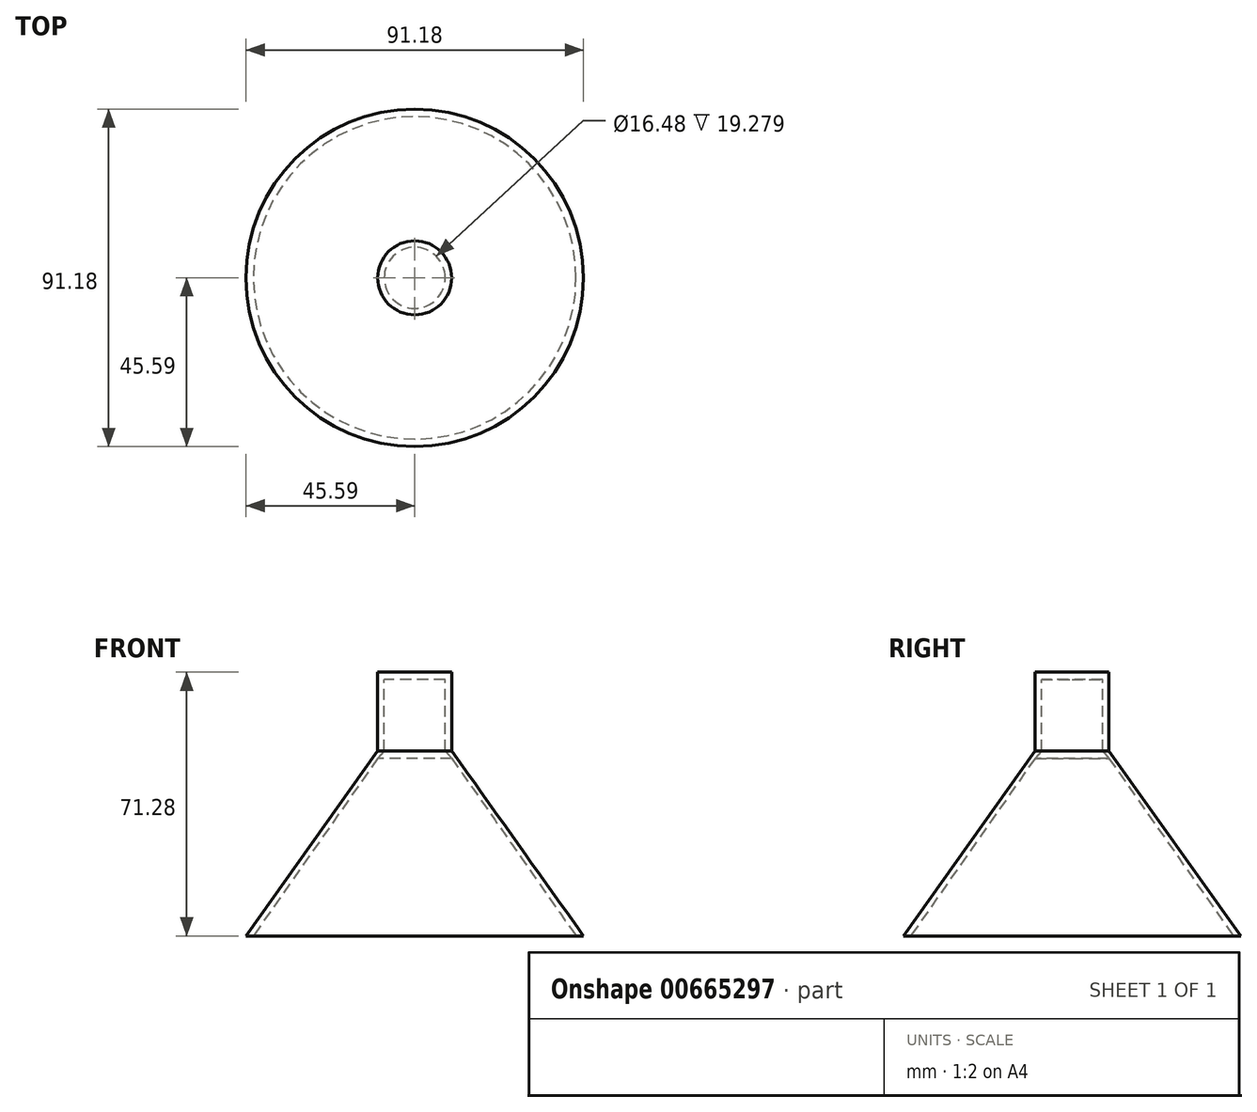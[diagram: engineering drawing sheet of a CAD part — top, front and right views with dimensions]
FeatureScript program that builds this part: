
annotation { "Feature Type Name" : "Feature", "Feature Type Description" : "" }
export const myFeature = defineFeature(function(context is Context, id is Id, definition is map)
    precondition{}
    {
        {
            var Q0;
            Q0=qCreatedBy(makeId("Front.planeOp"),FACE);
            var sketch = newSketch(context, id + "F0", { "sketchPlane" : qUnion([Q0])});
            skLineSegment(sketch, "E0", {"start": v(-10, 50) * mm, "end": v(-45.59, 0) * mm});
            skLineSegment(sketch, "E1", {"start": v(-45.59, 0) * mm, "end": v(-43.59, 0) * mm});
            skLineSegment(sketch, "E2", {"start": v(-10, 50) * mm, "end": v(-10, 48) * mm});
            skLineSegment(sketch, "E3", {"start": v(-43.59, 0) * mm, "end": v(-10, 48) * mm});
            skLineSegment(sketch, "E4", {"start": v(-10, 50) * mm, "end": v(-10, 71.28) * mm});
            skLineSegment(sketch, "E5", {"start": v(-10, 71.28) * mm, "end": v(0, 71.28) * mm});
            skLineSegment(sketch, "E6", {"start": v(0, 71.28) * mm, "end": v(0, 69.28) * mm});
            skLineSegment(sketch, "E7", {"start": v(0, 69.28) * mm, "end": v(-8.24, 69.28) * mm});
            skLineSegment(sketch, "E8", {"start": v(-8.24, 69.28) * mm, "end": v(-8.24, 50) * mm});
            skLineSegment(sketch, "E9", {"start": v(-8.24, 50) * mm, "end": v(-10, 48) * mm});
            skSolve(sketch);
        }
        {
            var Q0;
            Q0=makeQuery(id+"F0.imprint","IMPRINT",FACE,{"disambiguationData":[TD([[makeQuery(id+"F0.imprint","IMPRINT",EDGE,{"derivedFrom":sQuery(id+"F0.wireOp",EDGE,"E2")}),1.0]])]});
            var Q1;
            Q1=makeQuery(id+"F0.imprint","IMPRINT",FACE,{"disambiguationData":[TD([[makeQuery(id+"F0.imprint","IMPRINT",EDGE,{"derivedFrom":sQuery(id+"F0.wireOp",EDGE,"E0")}),1.0]])]});
            var Q2;
            Q2=sQuery(id+"F0.wireOp",EDGE,"E6");
            revolve(context, id + "F1", {"entities" : qUnion([Q0, Q1]), "axis" : qUnion([Q2]), "revolveType" : RevolveType.FULL});
        }
    });
